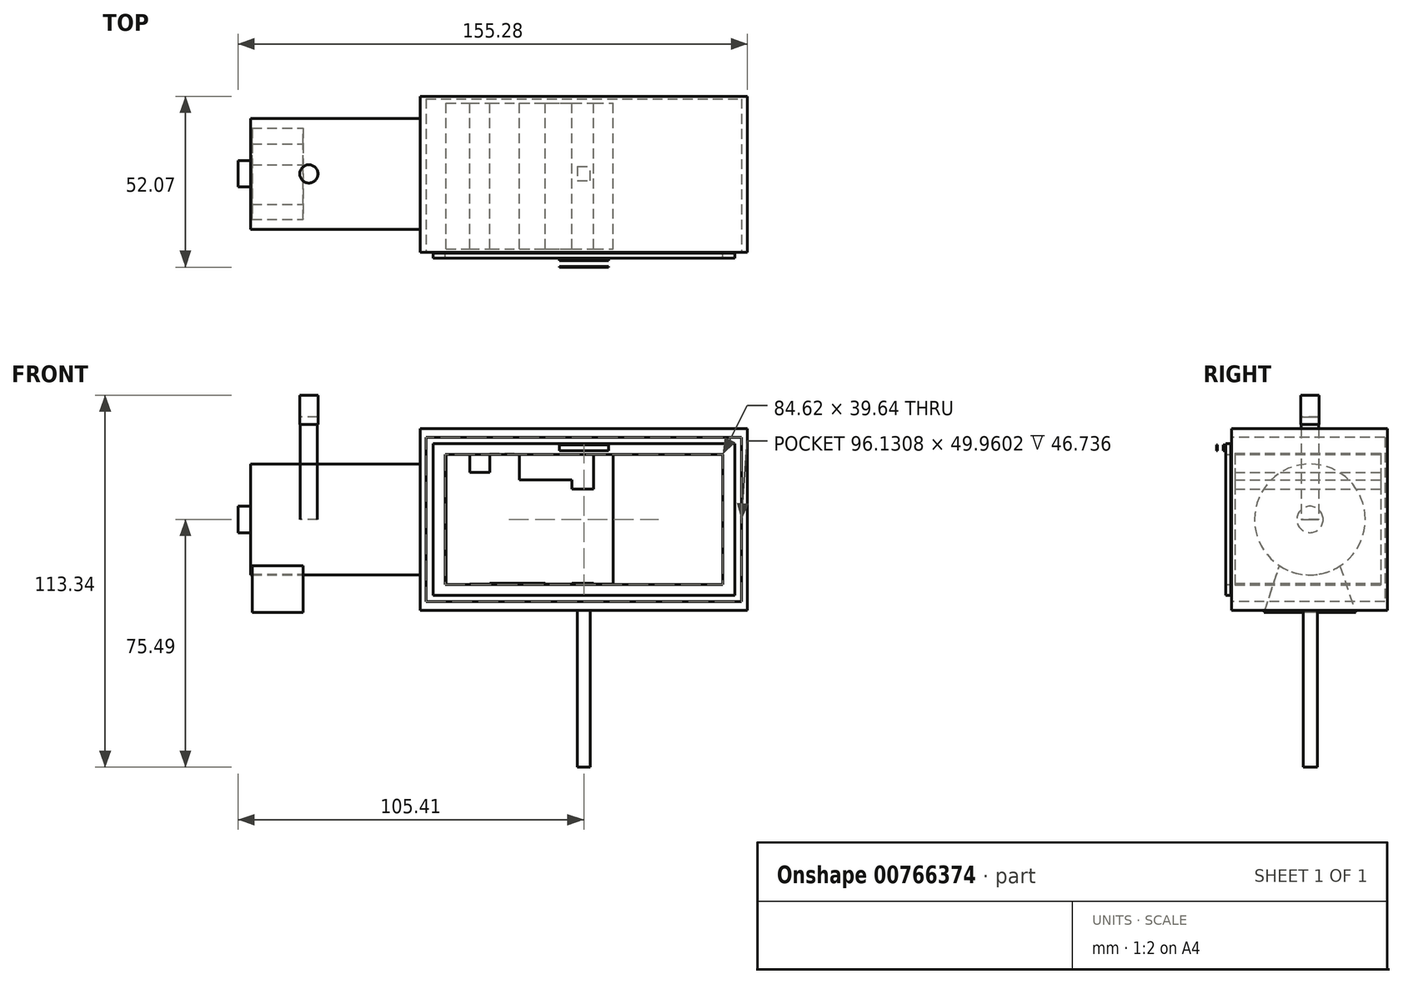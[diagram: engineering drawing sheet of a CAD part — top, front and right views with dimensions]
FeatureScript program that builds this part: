
annotation { "Feature Type Name" : "Feature", "Feature Type Description" : "" }
export const myFeature = defineFeature(function(context is Context, id is Id, definition is map)
    precondition{}
    {
        {
            var Q0;
            Q0=qCreatedBy(makeId("Front.planeOp"),FACE);
            var sketch = newSketch(context, id + "F0", { "sketchPlane" : qUnion([Q0])});
            skLineSegment(sketch, "E0.bottom", {"start": v(-49.87, 27.75) * mm, "end": v(49.87, 27.75) * mm});
            skLineSegment(sketch, "E0.top", {"start": v(-49.87, -27.75) * mm, "end": v(49.87, -27.75) * mm});
            skLineSegment(sketch, "E0.left", {"start": v(-49.87, 27.75) * mm, "end": v(-49.87, -27.75) * mm});
            skLineSegment(sketch, "E0.right", {"start": v(49.87, 27.75) * mm, "end": v(49.87, -27.75) * mm});
            skPoint(sketch, "E0.middle", {"position": v(0, 0) * mm});
            skLineSegment(sketch, "E1", {"start": v(0, 27.75) * mm, "end": v(0, -27.75) * mm});
            skSolve(sketch);
        }
        {
            var Q0;
            Q0=qCreatedBy(makeId("Front.planeOp"),FACE);
            var sketch = newSketch(context, id + "F1", { "sketchPlane" : qUnion([Q0])});
            skLineSegment(sketch, "E2.bottom", {"start": v(-46, -23.14) * mm, "end": v(46, -23.14) * mm});
            skLineSegment(sketch, "E2.top", {"start": v(-46, 23.14) * mm, "end": v(46, 23.14) * mm});
            skLineSegment(sketch, "E2.left", {"start": v(-46, -23.14) * mm, "end": v(-46, 23.14) * mm});
            skLineSegment(sketch, "E2.right", {"start": v(46, -23.14) * mm, "end": v(46, 23.14) * mm});
            skPoint(sketch, "E2.middle", {"position": v(0, 0) * mm});
            skLineSegment(sketch, "E3.bottom", {"start": v(-42.3, -19.82) * mm, "end": v(42.3, -19.82) * mm});
            skLineSegment(sketch, "E3.top", {"start": v(-42.3, 19.82) * mm, "end": v(42.3, 19.82) * mm});
            skLineSegment(sketch, "E3.left", {"start": v(-42.3, -19.82) * mm, "end": v(-42.3, 19.82) * mm});
            skLineSegment(sketch, "E3.right", {"start": v(42.3, -19.82) * mm, "end": v(42.3, 19.82) * mm});
            skSolve(sketch);
        }
        {
            var Q0;
            Q0=qCreatedBy(makeId("Right.planeOp"),FACE);
            var sketch = newSketch(context, id + "F2", { "sketchPlane" : qUnion([Q0])});
            skCircle(sketch, "E4", {"center": v(0, 0) * mm, "radius": 16.87 * mm});
            skSolve(sketch);
        }
        {
            var Q0;
            Q0=qCreatedBy(makeId("Right.planeOp"),FACE);
            var sketch = newSketch(context, id + "F3", { "sketchPlane" : qUnion([Q0])});
            skCircle(sketch, "E5", {"center": v(0, 0) * mm, "radius": 4.02 * mm});
            skSolve(sketch);
        }
        {
            var Q0;
            Q0=qCreatedBy(makeId("Right.planeOp"),FACE);
            var sketch = newSketch(context, id + "F4", { "sketchPlane" : qUnion([Q0])});
            skLineSegment(sketch, "E6", {"start": v(9.13, -14.1) * mm, "end": v(13.92, -28.3) * mm});
            skLineSegment(sketch, "E7", {"start": v(13.92, -28.3) * mm, "end": v(0, -28.3) * mm});
            skLineSegment(sketch, "E8", {"start": v(0, -28.3) * mm, "end": v(-13.92, -28.3) * mm});
            skLineSegment(sketch, "E9", {"start": v(-13.92, -28.3) * mm, "end": v(-9.3, -14.1) * mm});
            skArc(sketch, "E10", {"start": v(-9.3, -14.1) * mm, "mid": v(-0.1, -16.9) * mm, "end": v(9.13, -14.1) * mm});
            skSolve(sketch);
        }
        {
            var Q0;
            Q0=qCreatedBy(makeId("Top.planeOp"),FACE);
            var sketch = newSketch(context, id + "F5", { "sketchPlane" : qUnion([Q0])});
            skCircle(sketch, "E11", {"center": v(-83.79, 0) * mm, "radius": 2.78 * mm});
            skSolve(sketch);
        }
        {
            var Q0;
            Q0=qCreatedBy(makeId("Top.planeOp"),FACE);
            var sketch = newSketch(context, id + "F6", { "sketchPlane" : qUnion([Q0])});
            skCircle(sketch, "E12", {"center": v(-83.8, 0) * mm, "radius": 2.61 * mm});
            skSolve(sketch);
        }
        {
            var Q0;
            Q0=makeQuery(id+"F3.imprint","IMPRINT",FACE,{"disambiguationData":[TD([[makeQuery(id+"F3.imprint","IMPRINT",EDGE,{"derivedFrom":sQuery(id+"F3.wireOp",EDGE,"E5")}),1.0]])]});
            extrude(context, id + "F7", {"entities" : qUnion([Q0]), "oppositeDirection" : true, "depth" : 105.4 * mm, "offsetDistance" : 25.4 * mm, "hasSecondDirection" : true, "secondDirectionOppositeDirection" : true, "secondDirectionDepth" : 49.78 * mm});
        }
        {
            var Q0;
            Q0 = qSketchRegion(id + "F2", true);
            extrude(context, id + "F8", {"entities" : qUnion([Q0]), "operationType" : NewBodyOperationType.ADD, "oppositeDirection" : true, "depth" : 101.6 * mm, "offsetDistance" : 25.4 * mm, "hasSecondDirection" : true, "secondDirectionOppositeDirection" : true, "secondDirectionDepth" : 49.78 * mm});
        }
        {
            var Q0;
            Q0 = qSketchRegion(id + "F4", true);
            extrude(context, id + "F9", {"entities" : qUnion([Q0]), "operationType" : NewBodyOperationType.ADD, "oppositeDirection" : true, "depth" : 101.1 * mm, "offsetDistance" : 25.4 * mm, "hasSecondDirection" : true, "secondDirectionOppositeDirection" : true, "secondDirectionDepth" : 85.6 * mm});
        }
        {
            var Q0;
            Q0 = qSketchRegion(id + "F5", true);
            extrude(context, id + "F10", {"entities" : qUnion([Q0]), "depth" : 37.85 * mm, "offsetDistance" : 25.4 * mm, "hasSecondDirection" : true, "secondDirectionOppositeDirection" : false, "secondDirectionDepth" : 28.96 * mm});
        }
        {
            var Q0;
            Q0 = qSketchRegion(id + "F6", true);
            extrude(context, id + "F11", {"entities" : qUnion([Q0]), "depth" : 31.24 * mm, "offsetDistance" : 25.4 * mm});
        }
        {
            var Q0;
            Q0 = qSketchRegion(id + "F0", true);
            extrude(context, id + "F12", {"entities" : qUnion([Q0]), "operationType" : NewBodyOperationType.ADD, "depth" : 23.88 * mm, "offsetDistance" : 25.4 * mm, "hasSecondDirection" : true, "secondDirectionOppositeDirection" : true, "secondDirectionDepth" : 23.62 * mm});
        }
        {
            var Q0;
            Q0 = qSketchRegion(id + "F1", true);
            extrude(context, id + "F13", {"entities" : qUnion([Q0]), "operationType" : NewBodyOperationType.ADD, "depth" : 25.65 * mm, "offsetDistance" : 25.4 * mm});
        }
        {
            var Q0;
            Q0=qCreatedBy(makeId("Front.planeOp"),FACE);
            var sketch = newSketch(context, id + "F14", { "sketchPlane" : qUnion([Q0])});
            skLineSegment(sketch, "E13.bottom", {"start": v(-48.07, 24.98) * mm, "end": v(48.07, 24.98) * mm});
            skLineSegment(sketch, "E13.top", {"start": v(-48.07, -24.98) * mm, "end": v(48.07, -24.98) * mm});
            skLineSegment(sketch, "E13.left", {"start": v(-48.07, 24.98) * mm, "end": v(-48.07, -24.98) * mm});
            skLineSegment(sketch, "E13.right", {"start": v(48.07, 24.98) * mm, "end": v(48.07, -24.98) * mm});
            skPoint(sketch, "E13.middle", {"position": v(0, 0) * mm});
            skSolve(sketch);
        }
        {
            var Q0;
            Q0 = qSketchRegion(id + "F14", true);
            extrude(context, id + "F15", {"entities" : qUnion([Q0]), "operationType" : NewBodyOperationType.REMOVE, "oppositeDirection" : true, "depth" : 22.86 * mm, "offsetDistance" : 25.4 * mm, "hasSecondDirection" : true, "secondDirectionOppositeDirection" : false, "secondDirectionDepth" : 24.13 * mm});
        }
        {
            var Q0;
            Q0=qCreatedBy(makeId("Front.planeOp"),FACE);
            var sketch = newSketch(context, id + "F16", { "sketchPlane" : qUnion([Q0])});
            skLineSegment(sketch, "E14.bottom", {"start": v(-7.5, 20.92) * mm, "end": v(7.5, 20.92) * mm});
            skLineSegment(sketch, "E14.top", {"start": v(-7.5, 22.77) * mm, "end": v(7.5, 22.77) * mm});
            skLineSegment(sketch, "E14.left", {"start": v(-7.5, 20.92) * mm, "end": v(-7.5, 22.77) * mm});
            skLineSegment(sketch, "E14.right", {"start": v(7.5, 20.92) * mm, "end": v(7.5, 22.77) * mm});
            skPoint(sketch, "E14.middle", {"position": v(0, 21.85) * mm});
            skSolve(sketch);
        }
        {
            var Q0;
            Q0 = qSketchRegion(id + "F16", true);
            extrude(context, id + "F17", {"entities" : qUnion([Q0]), "operationType" : NewBodyOperationType.ADD, "depth" : 28.45 * mm, "offsetDistance" : 25.4 * mm, "hasSecondDirection" : true, "secondDirectionOppositeDirection" : false, "secondDirectionDepth" : 24.64 * mm});
        }
        {
            var Q0;
            Q0=qCreatedBy(makeId("Front.planeOp"),FACE);
            var sketch = newSketch(context, id + "F18", { "sketchPlane" : qUnion([Q0])});
            skLineSegment(sketch, "E15.bottom", {"start": v(-7.7, 22.95) * mm, "end": v(7.7, 22.95) * mm});
            skLineSegment(sketch, "E15.top", {"start": v(-7.7, 20.74) * mm, "end": v(7.7, 20.74) * mm});
            skLineSegment(sketch, "E15.left", {"start": v(-7.7, 22.95) * mm, "end": v(-7.7, 20.74) * mm});
            skLineSegment(sketch, "E15.right", {"start": v(7.7, 22.95) * mm, "end": v(7.7, 20.74) * mm});
            skPoint(sketch, "E15.middle", {"position": v(0, 21.85) * mm});
            skSolve(sketch);
        }
        {
            var Q0;
            Q0 = qSketchRegion(id + "F18", true);
            extrude(context, id + "F19", {"entities" : qUnion([Q0]), "operationType" : NewBodyOperationType.REMOVE, "depth" : 28.2 * mm, "offsetDistance" : 25.4 * mm, "hasSecondDirection" : true, "secondDirectionOppositeDirection" : false, "secondDirectionDepth" : 26.42 * mm});
        }
        {
            var Q0;
            Q0=qCreatedBy(makeId("Front.planeOp"),FACE);
            var sketch = newSketch(context, id + "F20", { "sketchPlane" : qUnion([Q0])});
            skLineSegment(sketch, "E16.bottom", {"start": v(-1.98, -75.5) * mm, "end": v(1.98, -75.5) * mm});
            skPoint(sketch, "E16.middle", {"position": v(0, -27.56) * mm});
            skLineSegment(sketch, "E17", {"start": v(-1.98, -27.56) * mm, "end": v(1.98, -27.56) * mm});
            skLineSegment(sketch, "E18", {"start": v(1.98, -75.5) * mm, "end": v(-1.98, -75.5) * mm});
            skLineSegment(sketch, "E19", {"start": v(-1.98, -75.5) * mm, "end": v(-1.98, -27.56) * mm});
            skLineSegment(sketch, "E20", {"start": v(1.98, -27.56) * mm, "end": v(1.98, -75.5) * mm});
            skLineSegment(sketch, "E21", {"start": v(1.98, -27.56) * mm, "end": v(-1.98, -27.56) * mm});
            skSolve(sketch);
        }
        {
            var Q0;
            Q0 = qSketchRegion(id + "F20", true);
            extrude(context, id + "F21", {"entities" : qUnion([Q0]), "operationType" : NewBodyOperationType.ADD, "depth" : 2.03 * mm, "offsetDistance" : 25.4 * mm, "hasSecondDirection" : true, "secondDirectionOppositeDirection" : true, "secondDirectionDepth" : 2.3 * mm});
        }
        {
            var Q0;
            Q0=qCreatedBy(makeId("Front.planeOp"),FACE);
            var sketch = newSketch(context, id + "F22", { "sketchPlane" : qUnion([Q0])});
            skLineSegment(sketch, "E22.bottom", {"start": v(-41.98, 20) * mm, "end": v(-34.8, 20) * mm});
            skLineSegment(sketch, "E22.top", {"start": v(-41.98, -20) * mm, "end": v(-34.8, -20) * mm});
            skLineSegment(sketch, "E22.left", {"start": v(-41.98, 20) * mm, "end": v(-41.98, -20) * mm});
            skLineSegment(sketch, "E22.right", {"start": v(-34.8, 20) * mm, "end": v(-34.8, -20) * mm});
            skLineSegment(sketch, "E23.bottom", {"start": v(-34.8, 14.29) * mm, "end": v(-28.7, 14.29) * mm});
            skLineSegment(sketch, "E23.top", {"start": v(-34.8, -19.63) * mm, "end": v(-28.7, -19.63) * mm});
            skLineSegment(sketch, "E23.left", {"start": v(-34.8, 14.29) * mm, "end": v(-34.8, -19.63) * mm});
            skLineSegment(sketch, "E23.right", {"start": v(-28.7, 14.29) * mm, "end": v(-28.7, -19.63) * mm});
            skLineSegment(sketch, "E24.bottom", {"start": v(-28.7, 20.19) * mm, "end": v(-19.67, 20.19) * mm});
            skLineSegment(sketch, "E24.top", {"start": v(-28.7, -19.45) * mm, "end": v(-19.67, -19.45) * mm});
            skLineSegment(sketch, "E24.left", {"start": v(-28.7, 20.19) * mm, "end": v(-28.7, -19.45) * mm});
            skLineSegment(sketch, "E24.right", {"start": v(-19.67, 20.19) * mm, "end": v(-19.67, -19.45) * mm});
            skLineSegment(sketch, "E25.bottom", {"start": v(-19.67, 12.08) * mm, "end": v(-11.75, 12.08) * mm});
            skLineSegment(sketch, "E25.top", {"start": v(-19.67, -19.45) * mm, "end": v(-11.75, -19.45) * mm});
            skLineSegment(sketch, "E25.left", {"start": v(-19.67, 12.08) * mm, "end": v(-19.67, -19.45) * mm});
            skLineSegment(sketch, "E25.right", {"start": v(-11.75, 12.08) * mm, "end": v(-11.75, -19.45) * mm});
            skLineSegment(sketch, "E26.bottom", {"start": v(-11.75, 12.08) * mm, "end": v(-3.64, 12.08) * mm});
            skLineSegment(sketch, "E26.top", {"start": v(-11.75, -19.63) * mm, "end": v(-3.64, -19.63) * mm});
            skLineSegment(sketch, "E26.left", {"start": v(-11.75, 12.08) * mm, "end": v(-11.75, -19.63) * mm});
            skLineSegment(sketch, "E26.right", {"start": v(-3.64, 12.08) * mm, "end": v(-3.64, -19.63) * mm});
            skLineSegment(sketch, "E27.bottom", {"start": v(-3.64, 9.3) * mm, "end": v(3, 9.3) * mm});
            skLineSegment(sketch, "E27.top", {"start": v(-3.64, -19.45) * mm, "end": v(3, -19.45) * mm});
            skLineSegment(sketch, "E27.left", {"start": v(-3.64, 9.3) * mm, "end": v(-3.64, -19.45) * mm});
            skLineSegment(sketch, "E27.right", {"start": v(3, 9.3) * mm, "end": v(3, -19.45) * mm});
            skLineSegment(sketch, "E28.bottom", {"start": v(3, 19.82) * mm, "end": v(8.9, 19.82) * mm});
            skLineSegment(sketch, "E28.top", {"start": v(3, -19.63) * mm, "end": v(8.9, -19.63) * mm});
            skLineSegment(sketch, "E28.left", {"start": v(3, 19.82) * mm, "end": v(3, -19.63) * mm});
            skLineSegment(sketch, "E28.right", {"start": v(8.9, 19.82) * mm, "end": v(8.9, -19.63) * mm});
            skSolve(sketch);
        }
        {
            var Q0;
            Q0 = qSketchRegion(id + "F22", true);
            extrude(context, id + "F23", {"entities" : qUnion([Q0]), "depth" : 22.86 * mm, "offsetDistance" : 25.4 * mm, "hasSecondDirection" : true, "secondDirectionOppositeDirection" : true, "secondDirectionDepth" : 21.59 * mm});
        }
    });
